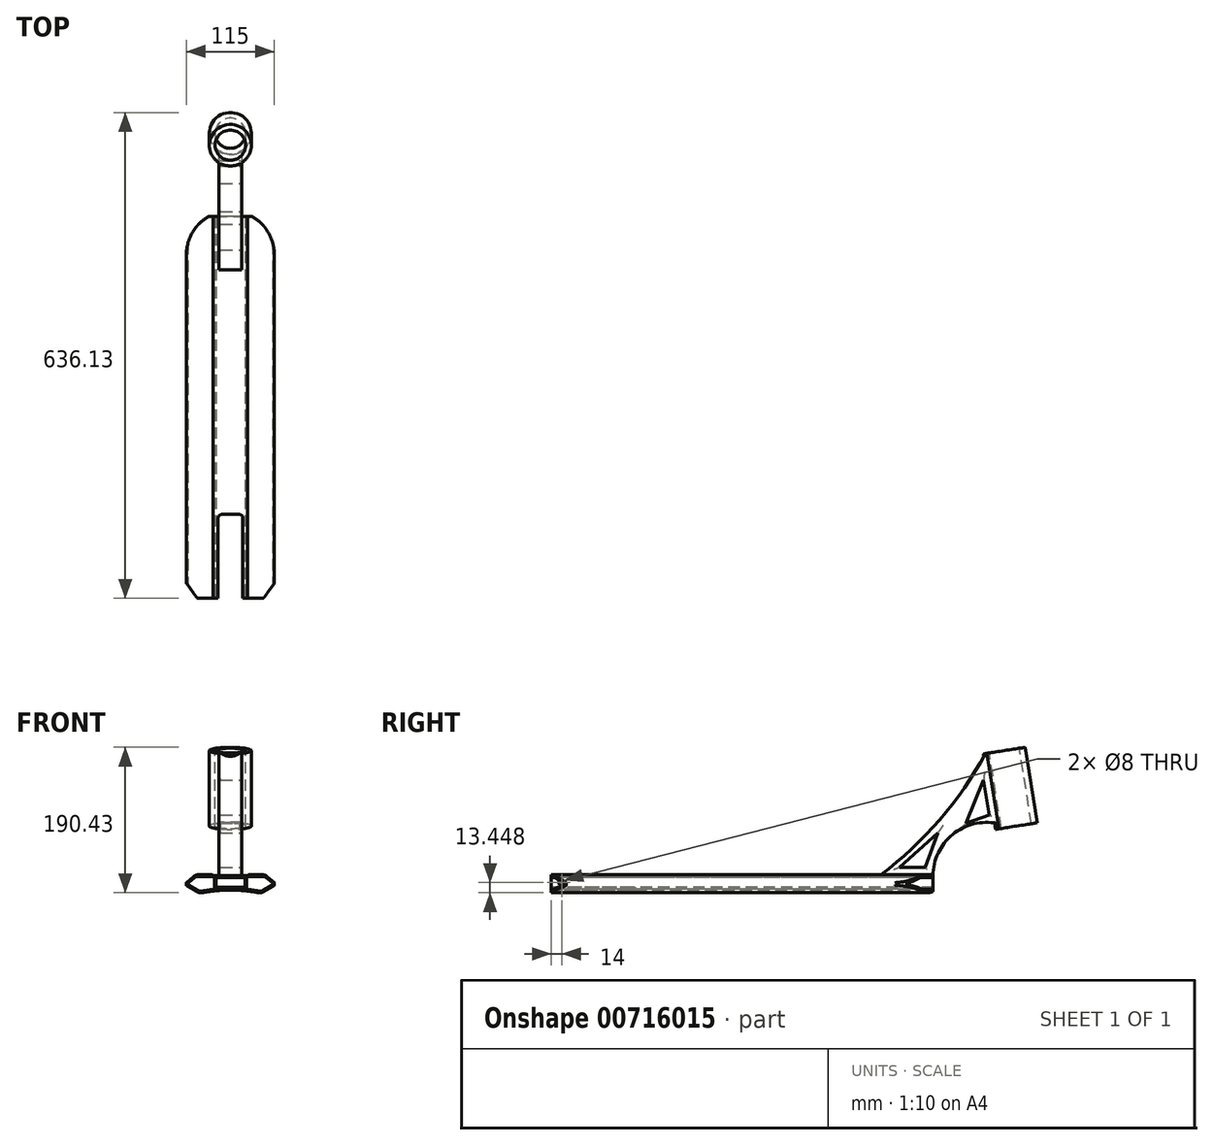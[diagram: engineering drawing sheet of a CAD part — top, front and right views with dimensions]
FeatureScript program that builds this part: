
annotation { "Feature Type Name" : "Feature", "Feature Type Description" : "" }
export const myFeature = defineFeature(function(context is Context, id is Id, definition is map)
    precondition{}
    {
        {
            var Q0;
            Q0=qCreatedBy(makeId("Front.planeOp"),FACE);
            var sketch = newSketch(context, id + "F0", { "sketchPlane" : qUnion([Q0])});
            skLineSegment(sketch, "E0", {"start": v(0, 0) * mm, "end": v(0, 25.65) * mm, "construction": true});
            skLineSegment(sketch, "E1", {"start": v(0, 15.2) * mm, "end": v(22.5, 15.2) * mm});
            skLineSegment(sketch, "E2", {"start": v(22.5, 15.2) * mm, "end": v(22.5, 16.5) * mm});
            skLineSegment(sketch, "E3", {"start": v(22.5, 16.5) * mm, "end": v(45.58, 16.5) * mm});
            skLineSegment(sketch, "E4", {"start": v(45.58, 16.5) * mm, "end": v(57.5, 6.5) * mm});
            skLineSegment(sketch, "E5", {"start": v(57.5, 6.5) * mm, "end": v(57.5, 2.5) * mm});
            skLineSegment(sketch, "E6", {"start": v(57.5, 2.5) * mm, "end": v(40.18, -7.5) * mm});
            skLineSegment(sketch, "E7.MirrorCS", {"start": v(0, 15.2) * mm, "end": v(-22.5, 15.2) * mm});
            skLineSegment(sketch, "E8.MirrorCS", {"start": v(-22.5, 16.5) * mm, "end": v(-45.58, 16.5) * mm});
            skLineSegment(sketch, "E9.MirrorCS", {"start": v(-45.58, 16.5) * mm, "end": v(-57.5, 6.5) * mm});
            skLineSegment(sketch, "E10.MirrorCS", {"start": v(-22.5, 15.2) * mm, "end": v(-22.5, 16.5) * mm});
            skLineSegment(sketch, "E11.MirrorCS", {"start": v(-57.5, 6.5) * mm, "end": v(-57.5, 2.5) * mm});
            skLineSegment(sketch, "E12.MirrorCS", {"start": v(-57.5, 2.5) * mm, "end": v(-40.18, -7.5) * mm});
            skArc(sketch, "E13", {"start": v(40.18, -7.5) * mm, "mid": v(0, -3.42) * mm, "end": v(-40.18, -7.5) * mm});
            skSolve(sketch);
        }
        {
            var Q0;
            Q0 = qSketchRegion(id + "F0", true);
            extrude(context, id + "F1", {"entities" : qUnion([Q0]), "depth" : 500 * mm, "offsetDistance" : 25 * mm, "symmetric" : true});
        }
        {
            var Q0;
            Q0=qCreatedBy(makeId("Front.planeOp"),FACE);
            var sketch = newSketch(context, id + "F2", { "sketchPlane" : qUnion([Q0])});
            skLineSegment(sketch, "E14.bottom", {"start": v(-19, 13.2) * mm, "end": v(19, 13.2) * mm});
            skLineSegment(sketch, "E14.top", {"start": v(-19, 0.2) * mm, "end": v(19, 0.2) * mm});
            skLineSegment(sketch, "E14.left", {"start": v(-19, 13.2) * mm, "end": v(-19, 0.2) * mm});
            skLineSegment(sketch, "E14.right", {"start": v(19, 13.2) * mm, "end": v(19, 0.2) * mm});
            skSolve(sketch);
        }
        {
            var Q0;
            Q0 = qSketchRegion(id + "F2", true);
            extrude(context, id + "F3", {"entities" : qUnion([Q0]), "operationType" : NewBodyOperationType.REMOVE, "oppositeDirection" : true, "depth" : 500 * mm, "offsetDistance" : 25 * mm, "symmetric" : true});
        }
        {
            var Q0;
            Q0=makeQuery(id+"F1.opExtrude","SWEPT_EDGE",EDGE,{"disambiguationData":[OSD([sQuery(id+"F0.wireOp",EDGE,"E8.MirrorCS"),sQuery(id+"F0.wireOp",EDGE,"E10.MirrorCS")])]});
            var Q1;
            Q1=makeQuery(id+"F1.opExtrude","SWEPT_EDGE",EDGE,{"disambiguationData":[OSD([sQuery(id+"F0.wireOp",EDGE,"E2"),sQuery(id+"F0.wireOp",EDGE,"E3")])]});
            fillet(context, id + "F4", {"entities" : qUnion([Q0, Q1]), "radius" : 2 * mm, "tangentPropagation" : true, "allowEdgeOverflow" : false});
        }
        {
            var Q0;
            Q0=makeQuery(id+"F1.opExtrude","SWEPT_EDGE",EDGE,{"disambiguationData":[OSD([sQuery(id+"F0.wireOp",EDGE,"E8.MirrorCS"),sQuery(id+"F0.wireOp",EDGE,"E9.MirrorCS")])]});
            var Q1;
            Q1=makeQuery(id+"F1.opExtrude","SWEPT_EDGE",EDGE,{"disambiguationData":[OSD([sQuery(id+"F0.wireOp",EDGE,"E3"),sQuery(id+"F0.wireOp",EDGE,"E4")])]});
            var Q2;
            Q2=makeQuery(id+"F1.opExtrude","SWEPT_EDGE",EDGE,{"disambiguationData":[OSD([sQuery(id+"F0.wireOp",EDGE,"E6"),sQuery(id+"F0.wireOp",EDGE,"E13")])]});
            var Q3;
            Q3=makeQuery(id+"F1.opExtrude","SWEPT_EDGE",EDGE,{"disambiguationData":[OSD([sQuery(id+"F0.wireOp",EDGE,"E12.MirrorCS"),sQuery(id+"F0.wireOp",EDGE,"E13")])]});
            fillet(context, id + "F5", {"entities" : qUnion([Q0, Q1, Q2, Q3]), "radius" : 9 * mm, "tangentPropagation" : true, "allowEdgeOverflow" : false});
        }
        {
            var Q0;
            Q0=makeQuery(id+"F1.opExtrude","SWEPT_EDGE",EDGE,{"disambiguationData":[OSD([sQuery(id+"F0.wireOp",EDGE,"E9.MirrorCS"),sQuery(id+"F0.wireOp",EDGE,"E11.MirrorCS")])]});
            var Q1;
            Q1=makeQuery(id+"F1.opExtrude","SWEPT_EDGE",EDGE,{"disambiguationData":[OSD([sQuery(id+"F0.wireOp",EDGE,"E11.MirrorCS"),sQuery(id+"F0.wireOp",EDGE,"E12.MirrorCS")])]});
            var Q2;
            Q2=makeQuery(id+"F1.opExtrude","SWEPT_EDGE",EDGE,{"disambiguationData":[OSD([sQuery(id+"F0.wireOp",EDGE,"E4"),sQuery(id+"F0.wireOp",EDGE,"E5")])]});
            var Q3;
            Q3=makeQuery(id+"F1.opExtrude","SWEPT_EDGE",EDGE,{"disambiguationData":[OSD([sQuery(id+"F0.wireOp",EDGE,"E5"),sQuery(id+"F0.wireOp",EDGE,"E6")])]});
            fillet(context, id + "F6", {"entities" : qUnion([Q0, Q1, Q2, Q3]), "radius" : 1 * mm, "tangentPropagation" : true, "allowEdgeOverflow" : false});
        }
        {
            var Q0;
            Q0=makeQuery(id+"F1.opExtrude","CAP_FACE",FACE,{"disambiguationData":[OSD([sQuery(id+"F0.wireOp",EDGE,"E1"),sQuery(id+"F0.wireOp",EDGE,"E2"),sQuery(id+"F0.wireOp",EDGE,"E3"),sQuery(id+"F0.wireOp",EDGE,"E4"),sQuery(id+"F0.wireOp",EDGE,"E5"),sQuery(id+"F0.wireOp",EDGE,"E6"),sQuery(id+"F0.wireOp",EDGE,"E7.MirrorCS"),sQuery(id+"F0.wireOp",EDGE,"E8.MirrorCS"),sQuery(id+"F0.wireOp",EDGE,"E9.MirrorCS"),sQuery(id+"F0.wireOp",EDGE,"E10.MirrorCS"),sQuery(id+"F0.wireOp",EDGE,"E11.MirrorCS"),sQuery(id+"F0.wireOp",EDGE,"E12.MirrorCS"),sQuery(id+"F0.wireOp",EDGE,"E13")])],"isStart":false});
            var sketch = newSketch(context, id + "F7", { "sketchPlane" : qUnion([Q0])});
            skLineSegment(sketch, "E15.0.0", {"start": v(-57.5, 6.04) * mm, "end": v(-57.5, 3.08) * mm});
            skArc(sketch, "E15.0.1", {"start": v(-57.5, 3.08) * mm, "mid": v(-57.37, 2.58) * mm, "end": v(-57, 2.22) * mm});
            skLineSegment(sketch, "E15.0.2", {"start": v(-57, 2.22) * mm, "end": v(-43.1, -5.8) * mm});
            skArc(sketch, "E15.0.3", {"start": v(-43.1, -5.8) * mm, "mid": v(-40.12, -6.88) * mm, "end": v(-36.94, -6.86) * mm});
            skArc(sketch, "E15.0.4", {"start": v(-36.94, -6.86) * mm, "mid": v(0, -3.42) * mm, "end": v(36.94, -6.86) * mm});
            skArc(sketch, "E15.0.5", {"start": v(36.94, -6.86) * mm, "mid": v(40.12, -6.88) * mm, "end": v(43.1, -5.8) * mm});
            skLineSegment(sketch, "E15.0.6", {"start": v(43.1, -5.8) * mm, "end": v(57, 2.22) * mm});
            skArc(sketch, "E15.0.7", {"start": v(57, 2.22) * mm, "mid": v(57.37, 2.58) * mm, "end": v(57.5, 3.08) * mm});
            skLineSegment(sketch, "E15.0.8", {"start": v(57.5, 3.08) * mm, "end": v(57.5, 6.04) * mm});
            skArc(sketch, "E15.0.9", {"start": v(57.5, 6.04) * mm, "mid": v(57.4, 6.46) * mm, "end": v(57.14, 6.8) * mm});
            skLineSegment(sketch, "E15.0.10", {"start": v(57.14, 6.8) * mm, "end": v(48.1, 14.4) * mm});
            skArc(sketch, "E15.0.11", {"start": v(48.1, 14.4) * mm, "mid": v(45.38, 15.96) * mm, "end": v(42.3, 16.5) * mm});
            skLineSegment(sketch, "E15.0.12", {"start": v(42.3, 16.5) * mm, "end": v(24.37, 16.5) * mm});
            skArc(sketch, "E15.0.13", {"start": v(24.37, 16.5) * mm, "mid": v(23.23, 16.15) * mm, "end": v(22.5, 15.2) * mm});
            skLineSegment(sketch, "E15.0.14", {"start": v(22.5, 15.2) * mm, "end": v(-22.5, 15.2) * mm});
            skArc(sketch, "E15.0.15", {"start": v(-22.5, 15.2) * mm, "mid": v(-23.23, 16.15) * mm, "end": v(-24.37, 16.5) * mm});
            skLineSegment(sketch, "E15.0.16", {"start": v(-24.37, 16.5) * mm, "end": v(-42.3, 16.5) * mm});
            skArc(sketch, "E15.0.17", {"start": v(-42.3, 16.5) * mm, "mid": v(-45.38, 15.96) * mm, "end": v(-48.1, 14.4) * mm});
            skLineSegment(sketch, "E15.0.18", {"start": v(-48.1, 14.4) * mm, "end": v(-57.14, 6.8) * mm});
            skArc(sketch, "E15.0.19", {"start": v(-57.14, 6.8) * mm, "mid": v(-57.4, 6.46) * mm, "end": v(-57.5, 6.04) * mm});
            skArc(sketch, "E16.0", {"start": v(-37.3, -4.9) * mm, "mid": v(0, -1.42) * mm, "end": v(37.3, -4.9) * mm});
            skArc(sketch, "E16.1", {"start": v(-42.1, -4.07) * mm, "mid": v(-39.78, -4.91) * mm, "end": v(-37.3, -4.9) * mm});
            skLineSegment(sketch, "E16.2", {"start": v(-24.37, 14.5) * mm, "end": v(-42.3, 14.5) * mm});
            skArc(sketch, "E16.3", {"start": v(-42.3, 14.5) * mm, "mid": v(-44.7, 14.08) * mm, "end": v(-46.8, 12.87) * mm});
            skLineSegment(sketch, "E16.4", {"start": v(-46.8, 12.87) * mm, "end": v(-54.66, 6.28) * mm});
            skLineSegment(sketch, "E16.5", {"start": v(-54.38, 3.01) * mm, "end": v(-42.1, -4.07) * mm});
            skLineSegment(sketch, "E17.0", {"start": v(-21, 15.2) * mm, "end": v(-21, -2.5) * mm});
            skLineSegment(sketch, "E17.1", {"start": v(-21, 15.2) * mm, "end": v(19, 15.2) * mm});
            skLineSegment(sketch, "E18.0", {"start": v(22.5, 13.2) * mm, "end": v(-22.5, 13.2) * mm});
            skArc(sketch, "E19", {"start": v(-22.5, 13.2) * mm, "mid": v(-23.23, 14.15) * mm, "end": v(-24.37, 14.5) * mm});
            skPoint(sketch, "E20.visualSharp", {"position": v(-56.85, 4.44) * mm});
            skArc(sketch, "E20.filletArc", {"start": v(-54.66, 6.28) * mm, "mid": v(-55.37, 4.57) * mm, "end": v(-54.38, 3.01) * mm});
            skLineSegment(sketch, "E21.MirrorCS", {"start": v(21, 15.2) * mm, "end": v(21, -2.5) * mm});
            skLineSegment(sketch, "E22.MirrorCS", {"start": v(24.37, 14.5) * mm, "end": v(42.3, 14.5) * mm});
            skArc(sketch, "E23.MirrorCS", {"start": v(42.3, 14.5) * mm, "mid": v(44.7, 14.08) * mm, "end": v(46.8, 12.87) * mm});
            skLineSegment(sketch, "E24.MirrorCS", {"start": v(46.8, 12.87) * mm, "end": v(54.66, 6.28) * mm});
            skArc(sketch, "E25.MirrorCS", {"start": v(54.66, 6.28) * mm, "mid": v(55.37, 4.57) * mm, "end": v(54.38, 3.01) * mm});
            skLineSegment(sketch, "E26.MirrorCS", {"start": v(54.38, 3.01) * mm, "end": v(42.1, -4.07) * mm});
            skArc(sketch, "E27.MirrorCS", {"start": v(42.1, -4.07) * mm, "mid": v(39.78, -4.91) * mm, "end": v(37.3, -4.9) * mm});
            skArc(sketch, "E28.MirrorCS", {"start": v(22.5, 13.2) * mm, "mid": v(23.23, 14.15) * mm, "end": v(24.37, 14.5) * mm});
            skSolve(sketch);
        }
        {
            var Q0;
            {var subQ4=sQuery(id+"F7.wireOp",EDGE,"E16.1");Q0=makeQuery(id+"F7.imprint","IMPRINT",FACE,{"disambiguationData":[TD([[makeQuery(id+"F7.imprint","IMPRINT",EDGE,{"derivedFrom":subQ4}),1.0]])]});}
            var Q1;
            Q1=makeQuery(id+"F7.imprint","IMPRINT",FACE,{"disambiguationData":[TD([[makeQuery(id+"F7.imprint","IMPRINT",EDGE,{"derivedFrom":sQuery(id+"F7.wireOp",EDGE,"E22.MirrorCS")}),-1.0]])]});
            extrude(context, id + "F8", {"entities" : qUnion([Q0, Q1]), "operationType" : NewBodyOperationType.REMOVE, "endBound" : BoundingType.THROUGH_ALL, "oppositeDirection" : true, "depth" : 25 * mm, "offsetDistance" : 25 * mm});
        }
        {
            var Q0;
            Q0=qCreatedBy(makeId("Top.planeOp"),FACE);
            var sketch = newSketch(context, id + "F9", { "sketchPlane" : qUnion([Q0])});
            skArc(sketch, "E29", {"start": v(57.5, 200) * mm, "mid": v(0, 257.5) * mm, "end": v(-57.5, 200) * mm});
            skLineSegment(sketch, "E30", {"start": v(-69.76, 280) * mm, "end": v(97.22, 280) * mm});
            skLineSegment(sketch, "E31", {"start": v(57.5, 200) * mm, "end": v(57.5, 280) * mm});
            skLineSegment(sketch, "E32", {"start": v(-57.5, 200) * mm, "end": v(-57.5, 280) * mm});
            skSolve(sketch);
        }
        {
            var Q0;
            Q0 = qSketchRegion(id + "F9", true);
            extrude(context, id + "F10", {"entities" : qUnion([Q0]), "operationType" : NewBodyOperationType.REMOVE, "endBound" : BoundingType.THROUGH_ALL, "oppositeDirection" : true, "depth" : 25 * mm, "offsetDistance" : 25 * mm, "hasSecondDirection" : true, "secondDirectionBound" : BoundingType.THROUGH_ALL, "secondDirectionOppositeDirection" : false, "secondDirectionDepth" : 25 * mm});
        }
        {
            var Q0;
            Q0=qCreatedBy(makeId("Top.planeOp"),FACE);
            var sketch = newSketch(context, id + "F11", { "sketchPlane" : qUnion([Q0])});
            skLineSegment(sketch, "E33", {"start": v(-68, -216) * mm, "end": v(-68, -346) * mm});
            skLineSegment(sketch, "E34", {"start": v(68, -346) * mm, "end": v(68, -216) * mm});
            skLineSegment(sketch, "E35", {"start": v(68, -216) * mm, "end": v(43.3, -250) * mm});
            skLineSegment(sketch, "E36", {"start": v(43.3, -250) * mm, "end": v(16.39, -250) * mm});
            skLineSegment(sketch, "E37", {"start": v(0.39, -140) * mm, "end": v(-16, -140) * mm});
            skLineSegment(sketch, "E38", {"start": v(-16, -140) * mm, "end": v(-16, -250) * mm});
            skLineSegment(sketch, "E39", {"start": v(-68, -216) * mm, "end": v(-43.3, -250) * mm});
            skLineSegment(sketch, "E40", {"start": v(-68, -346) * mm, "end": v(0, -346) * mm});
            skLineSegment(sketch, "E41", {"start": v(0, -346) * mm, "end": v(68, -346) * mm});
            skLineSegment(sketch, "E42", {"start": v(0.39, -140) * mm, "end": v(16.39, -140) * mm});
            skLineSegment(sketch, "E43", {"start": v(16.39, -140) * mm, "end": v(16.39, -250) * mm});
            skLineSegment(sketch, "E44", {"start": v(-43.3, -250) * mm, "end": v(-16, -250) * mm});
            skSolve(sketch);
        }
        {
            var Q0;
            Q0 = qSketchRegion(id + "F11", true);
            extrude(context, id + "F12", {"entities" : qUnion([Q0]), "operationType" : NewBodyOperationType.REMOVE, "endBound" : BoundingType.THROUGH_ALL, "depth" : 25 * mm, "offsetDistance" : 25 * mm, "hasSecondDirection" : true, "secondDirectionBound" : BoundingType.THROUGH_ALL, "secondDirectionOppositeDirection" : true, "secondDirectionDepth" : 25 * mm});
        }
        {
            var Q0;
            {var subQ0=sQuery(id+"F11.wireOp",EDGE,"E38");var subQ1=sQuery(id+"F11.wireOp",EDGE,"E37");Q0=makeQuery(id+"F12.boolean.opBoolean","COPY",EDGE,{"disambiguationData":[TD([makeQuery(id+"F3.boolean.opBoolean","COPY",FACE,{"derivedFrom":makeQuery(id+"F3.opExtrude","SWEPT_FACE",FACE,{"disambiguationData":[OSD([sQuery(id+"F2.wireOp",EDGE,"E14.bottom")])]})})])],"derivedFrom":makeQuery(id+"F12.opExtrude","SWEPT_EDGE",EDGE,{"disambiguationData":[OSD([subQ1,subQ0])]})});}
            var Q1;
            {var subQ0=sQuery(id+"F11.wireOp",EDGE,"E42");var subQ1=sQuery(id+"F11.wireOp",EDGE,"E43");Q1=makeQuery(id+"F12.boolean.opBoolean","COPY",EDGE,{"disambiguationData":[TD([makeQuery(id+"F3.boolean.opBoolean","COPY",FACE,{"derivedFrom":makeQuery(id+"F3.opExtrude","SWEPT_FACE",FACE,{"disambiguationData":[OSD([sQuery(id+"F2.wireOp",EDGE,"E14.bottom")])]})})])],"derivedFrom":makeQuery(id+"F12.opExtrude","SWEPT_EDGE",EDGE,{"disambiguationData":[OSD([subQ0,subQ1])]})});}
            var Q2;
            {var subQ2=sQuery(id+"F11.wireOp",EDGE,"E43");Q2=makeQuery(id+"F12.boolean.opBoolean","COPY",EDGE,{"disambiguationData":[TD([makeQuery(id+"F3.boolean.opBoolean","COPY",FACE,{"derivedFrom":makeQuery(id+"F3.opExtrude","SWEPT_FACE",FACE,{"disambiguationData":[OSD([sQuery(id+"F2.wireOp",EDGE,"E14.bottom")])]})})])],"derivedFrom":makeQuery(id+"F12.opExtrude","SWEPT_EDGE",EDGE,{"disambiguationData":[OSD([sQuery(id+"F11.wireOp",EDGE,"E36"),subQ2])]})});}
            var Q3;
            {var subQ2=sQuery(id+"F11.wireOp",EDGE,"E38");Q3=makeQuery(id+"F12.boolean.opBoolean","COPY",EDGE,{"disambiguationData":[TD([makeQuery(id+"F3.boolean.opBoolean","COPY",FACE,{"derivedFrom":makeQuery(id+"F3.opExtrude","SWEPT_FACE",FACE,{"disambiguationData":[OSD([sQuery(id+"F2.wireOp",EDGE,"E14.bottom")])]})})])],"derivedFrom":makeQuery(id+"F12.opExtrude","SWEPT_EDGE",EDGE,{"disambiguationData":[OSD([subQ2,sQuery(id+"F11.wireOp",EDGE,"E44")])]})});}
            var Q4;
            {var subQ0=sQuery(id+"F11.wireOp",EDGE,"E43");var subQ1=sQuery(id+"F11.wireOp",EDGE,"E42");Q4=makeQuery(id+"F12.boolean.opBoolean","COPY",EDGE,{"disambiguationData":[TD([makeQuery(id+"F1.opExtrude","SWEPT_FACE",FACE,{"disambiguationData":[OSD([sQuery(id+"F0.wireOp",EDGE,"E13")])]})])],"derivedFrom":makeQuery(id+"F12.opExtrude","SWEPT_EDGE",EDGE,{"disambiguationData":[OSD([subQ1,subQ0])]})});}
            var Q5;
            {var subQ0=sQuery(id+"F11.wireOp",EDGE,"E37");var subQ1=sQuery(id+"F11.wireOp",EDGE,"E38");Q5=makeQuery(id+"F12.boolean.opBoolean","COPY",EDGE,{"disambiguationData":[TD([makeQuery(id+"F1.opExtrude","SWEPT_FACE",FACE,{"disambiguationData":[OSD([sQuery(id+"F0.wireOp",EDGE,"E13")])]})])],"derivedFrom":makeQuery(id+"F12.opExtrude","SWEPT_EDGE",EDGE,{"disambiguationData":[OSD([subQ0,subQ1])]})});}
            fillet(context, id + "F13", {"entities" : qUnion([Q0, Q1, Q2, Q3, Q4, Q5]), "radius" : 5 * mm, "tangentPropagation" : true, "allowEdgeOverflow" : false});
        }
        {
            var Q0;
            Q0=qCreatedBy(makeId("Right.planeOp"),FACE);
            var sketch = newSketch(context, id + "F14", { "sketchPlane" : qUnion([Q0])});
            skLineSegment(sketch, "E45", {"start": v(180, 16.5) * mm, "end": v(250, 16.5) * mm});
            skLineSegment(sketch, "E46", {"start": v(333.69, 85.16) * mm, "end": v(334.85, 77.83) * mm});
            skLineSegment(sketch, "E47", {"start": v(334.85, 77.83) * mm, "end": v(381.69, 85.25) * mm});
            skArc(sketch, "E48", {"start": v(333.69, 85.16) * mm, "mid": v(275.6, 70.63) * mm, "end": v(250, 16.5) * mm});
            skLineSegment(sketch, "E49", {"start": v(381.69, 85.25) * mm, "end": v(366.04, 184.02) * mm});
            skLineSegment(sketch, "E50", {"start": v(366.04, 184.02) * mm, "end": v(318.63, 176.5) * mm});
            skArc(sketch, "E51", {"start": v(180, 16.5) * mm, "mid": v(257.88, 89.09) * mm, "end": v(318.63, 176.5) * mm});
            skSolve(sketch);
        }
        {
            var Q0;
            Q0 = qSketchRegion(id + "F14", true);
            extrude(context, id + "F15", {"entities" : qUnion([Q0]), "operationType" : NewBodyOperationType.ADD, "depth" : 30 * mm, "offsetDistance" : 25 * mm, "symmetric" : true});
        }
        {
            var Q0;
            Q0=makeQuery(id+"F15.opExtrude","SWEPT_FACE",FACE,{"disambiguationData":[OSD([sQuery(id+"F14.wireOp",EDGE,"E50")])]});
            var sketch = newSketch(context, id + "F16", { "sketchPlane" : qUnion([Q0])});
            skCircle(sketch, "E52", {"center": v(0, 367.32) * mm, "radius": 27.5 * mm});
            skSolve(sketch);
        }
        {
            var Q0;
            Q0 = qSketchRegion(id + "F16", true);
            var Q1;
            Q1=makeQuery(id+"F15.opExtrude","SWEPT_FACE",FACE,{"disambiguationData":[OSD([sQuery(id+"F14.wireOp",EDGE,"E47")])]});
            extrude(context, id + "F17", {"entities" : qUnion([Q0]), "operationType" : NewBodyOperationType.ADD, "endBound" : BoundingType.UP_TO_SURFACE, "oppositeDirection" : true, "depth" : 25 * mm, "endBoundEntityFace" : qUnion([Q1]), "offsetDistance" : 25 * mm});
        }
        {
            var Q0;
            Q0=makeQuery(id+"F17.boolean.opBoolean","MERGE",FACE,{"derivedFrom":[makeQuery(id+"F15.opExtrude","SWEPT_FACE",FACE,{"disambiguationData":[OSD([sQuery(id+"F14.wireOp",EDGE,"E50")])]}),makeQuery(id+"F17.opExtrude","CAP_FACE",FACE,{"disambiguationData":[OSD([sQuery(id+"F16.wireOp",EDGE,"E52")])],"isStart":true})]});
            var sketch = newSketch(context, id + "F18", { "sketchPlane" : qUnion([Q0])});
            skPoint(sketch, "E53", {"position": v(0, 367.32) * mm});
            skSolve(sketch);
        }
        {
            var Q0;
            Q0=sQuery(id+"F18.wireOp",VERTEX,"E53");
            var Q1;
            Q1=makeQuery(id+"F15.opExtrude","SWEPT_BODY",BODY,{"disambiguationData":[OSD([sQuery(id+"F14.wireOp",EDGE,"E45"),sQuery(id+"F14.wireOp",EDGE,"E46"),sQuery(id+"F14.wireOp",EDGE,"E47"),sQuery(id+"F14.wireOp",EDGE,"E48"),sQuery(id+"F14.wireOp",EDGE,"E49"),sQuery(id+"F14.wireOp",EDGE,"E50"),sQuery(id+"F14.wireOp",EDGE,"E51")])]});
            hole(context, id + "F19", {"style" : HoleStyle.SIMPLE, "endStyle" : HoleEndStyle.THROUGH, "holeDiameter" : 40 * mm, "majorDiameter" : 5 * mm, "isTappedThrough" : true, "tappedDepth" : 12 * mm, "tapClearance" : 3, "locations" : qUnion([Q0]), "scope" : qUnion([Q1])});
        }
        {
            var Q0;
            Q0=makeQuery(id+"F15.opExtrude","SWEPT_FACE",FACE,{"disambiguationData":[OSD([sQuery(id+"F14.wireOp",EDGE,"E45")])]});
            var Q1;
            Q1=makeQuery(id+"F1.opExtrude","SWEPT_FACE",FACE,{"disambiguationData":[OSD([sQuery(id+"F0.wireOp",EDGE,"E1"),sQuery(id+"F0.wireOp",EDGE,"E7.MirrorCS")])]});
            extrude(context, id + "F20", {"entities" : qUnion([Q0]), "endBound" : BoundingType.UP_TO_SURFACE, "depth" : 25 * mm, "endBoundEntityFace" : qUnion([Q1]), "offsetDistance" : 25 * mm});
        }
        {
            var Q0;
            Q0=makeQuery(id+"F20.opExtrude","SWEPT_BODY",BODY,{"disambiguationData":[OSD([sQuery(id+"F14.wireOp",EDGE,"E45")])]});
            deleteBodies(context, id + "F21", {"entities" : qUnion([Q0])});
        }
        {
            var Q0;
            Q0=makeQuery(id+"F15.opExtrude","SWEPT_BODY",BODY,{"disambiguationData":[OSD([sQuery(id+"F14.wireOp",EDGE,"E45"),sQuery(id+"F14.wireOp",EDGE,"E46"),sQuery(id+"F14.wireOp",EDGE,"E47"),sQuery(id+"F14.wireOp",EDGE,"E48"),sQuery(id+"F14.wireOp",EDGE,"E49"),sQuery(id+"F14.wireOp",EDGE,"E50"),sQuery(id+"F14.wireOp",EDGE,"E51")])]});
            transform(context, id + "F22", {"entities" : qUnion([Q0]), "transformType" : TransformType.TRANSLATION_3D, "dx" : 0 * mm, "dy" : 0 * mm, "dz" : -1.3 * mm, "makeCopy" : false});
        }
        {
            var Q0;
            Q0=makeQuery(id+"F8.boolean.opBoolean","COPY",FACE,{"derivedFrom":makeQuery(id+"F8.opExtrude","SWEPT_FACE",FACE,{"disambiguationData":[OSD([sQuery(id+"F7.wireOp",EDGE,"E21.MirrorCS")])]})});
            var sketch = newSketch(context, id + "F23", { "sketchPlane" : qUnion([Q0])});
            skPoint(sketch, "E54", {"position": v(-236, 6.44) * mm});
            skSolve(sketch);
        }
        {
            var Q0;
            Q0=sQuery(id+"F23.wireOp",VERTEX,"E54");
            var Q1;
            Q1=makeQuery(id+"F1.opExtrude","SWEPT_BODY",BODY,{"disambiguationData":[OSD([sQuery(id+"F0.wireOp",EDGE,"E1"),sQuery(id+"F0.wireOp",EDGE,"E2"),sQuery(id+"F0.wireOp",EDGE,"E3"),sQuery(id+"F0.wireOp",EDGE,"E4"),sQuery(id+"F0.wireOp",EDGE,"E5"),sQuery(id+"F0.wireOp",EDGE,"E6"),sQuery(id+"F0.wireOp",EDGE,"E7.MirrorCS"),sQuery(id+"F0.wireOp",EDGE,"E8.MirrorCS"),sQuery(id+"F0.wireOp",EDGE,"E9.MirrorCS"),sQuery(id+"F0.wireOp",EDGE,"E10.MirrorCS"),sQuery(id+"F0.wireOp",EDGE,"E11.MirrorCS"),sQuery(id+"F0.wireOp",EDGE,"E12.MirrorCS"),sQuery(id+"F0.wireOp",EDGE,"E13")])]});
            hole(context, id + "F24", {"style" : HoleStyle.SIMPLE, "endStyle" : HoleEndStyle.BLIND, "holeDiameter" : 8 * mm, "majorDiameter" : 5 * mm, "holeDepth" : 50 * mm, "isTappedThrough" : true, "tappedDepth" : 12 * mm, "tapClearance" : 3, "locations" : qUnion([Q0]), "scope" : qUnion([Q1])});
        }
        {
            var Q0;
            Q0=makeQuery(id+"F15.opExtrude","CAP_FACE",FACE,{"disambiguationData":[OSD([sQuery(id+"F14.wireOp",EDGE,"E45"),sQuery(id+"F14.wireOp",EDGE,"E46"),sQuery(id+"F14.wireOp",EDGE,"E47"),sQuery(id+"F14.wireOp",EDGE,"E48"),sQuery(id+"F14.wireOp",EDGE,"E49"),sQuery(id+"F14.wireOp",EDGE,"E50"),sQuery(id+"F14.wireOp",EDGE,"E51")])],"isStart":false});
            var sketch = newSketch(context, id + "F25", { "sketchPlane" : qUnion([Q0])});
            skLineSegment(sketch, "E55", {"start": v(206, 26.5) * mm, "end": v(256.38, 71.5) * mm});
            skLineSegment(sketch, "E56", {"start": v(256.38, 71.5) * mm, "end": v(240, 26.5) * mm});
            skLineSegment(sketch, "E57", {"start": v(240, 26.5) * mm, "end": v(206, 26.5) * mm});
            skLineSegment(sketch, "E58", {"start": v(316.02, 140.25) * mm, "end": v(323.2, 94.93) * mm});
            skLineSegment(sketch, "E59", {"start": v(323.2, 94.93) * mm, "end": v(293.2, 83.86) * mm});
            skLineSegment(sketch, "E60", {"start": v(293.2, 83.86) * mm, "end": v(316.02, 140.25) * mm});
            skSolve(sketch);
        }
        {
            var Q0;
            Q0=makeQuery(id+"F25.imprint","IMPRINT",FACE,{"disambiguationData":[TD([[makeQuery(id+"F25.imprint","IMPRINT",EDGE,{"derivedFrom":sQuery(id+"F25.wireOp",EDGE,"E58")}),-1.0]])]});
            var Q1;
            Q1=makeQuery(id+"F25.imprint","IMPRINT",FACE,{"disambiguationData":[TD([[makeQuery(id+"F25.imprint","IMPRINT",EDGE,{"derivedFrom":sQuery(id+"F25.wireOp",EDGE,"E55")}),-1.0]])]});
            extrude(context, id + "F26", {"entities" : qUnion([Q0, Q1]), "operationType" : NewBodyOperationType.REMOVE, "endBound" : BoundingType.THROUGH_ALL, "oppositeDirection" : true, "depth" : 25 * mm, "offsetDistance" : 25 * mm});
        }
        {
            var Q0;
            Q0=makeQuery(id+"F26.boolean.opBoolean","COPY",EDGE,{"derivedFrom":makeQuery(id+"F26.opExtrude","CAP_EDGE",EDGE,{"disambiguationData":[OSD([sQuery(id+"F25.wireOp",EDGE,"E59")])],"isStart":true})});
            var Q1;
            Q1=makeQuery(id+"F26.boolean.opBoolean","COPY",EDGE,{"derivedFrom":makeQuery(id+"F26.opExtrude","CAP_EDGE",EDGE,{"disambiguationData":[OSD([sQuery(id+"F25.wireOp",EDGE,"E58")])],"isStart":true})});
            var Q2;
            Q2=makeQuery(id+"F26.boolean.opBoolean","COPY",EDGE,{"derivedFrom":makeQuery(id+"F26.opExtrude","CAP_EDGE",EDGE,{"disambiguationData":[OSD([sQuery(id+"F25.wireOp",EDGE,"E60")])],"isStart":true})});
            var Q3;
            Q3=makeQuery(id+"F26.boolean.opBoolean","INTERSECT",EDGE,{"derivedFrom":[makeQuery(id+"F15.opExtrude","CAP_FACE",FACE,{"disambiguationData":[OSD([sQuery(id+"F14.wireOp",EDGE,"E45"),sQuery(id+"F14.wireOp",EDGE,"E46"),sQuery(id+"F14.wireOp",EDGE,"E47"),sQuery(id+"F14.wireOp",EDGE,"E48"),sQuery(id+"F14.wireOp",EDGE,"E49"),sQuery(id+"F14.wireOp",EDGE,"E50"),sQuery(id+"F14.wireOp",EDGE,"E51")])],"isStart":true}),makeQuery(id+"F26.opExtrude","SWEPT_FACE",FACE,{"disambiguationData":[OSD([sQuery(id+"F25.wireOp",EDGE,"E59")])]})]});
            var Q4;
            Q4=makeQuery(id+"F26.boolean.opBoolean","INTERSECT",EDGE,{"derivedFrom":[makeQuery(id+"F15.opExtrude","CAP_FACE",FACE,{"disambiguationData":[OSD([sQuery(id+"F14.wireOp",EDGE,"E45"),sQuery(id+"F14.wireOp",EDGE,"E46"),sQuery(id+"F14.wireOp",EDGE,"E47"),sQuery(id+"F14.wireOp",EDGE,"E48"),sQuery(id+"F14.wireOp",EDGE,"E49"),sQuery(id+"F14.wireOp",EDGE,"E50"),sQuery(id+"F14.wireOp",EDGE,"E51")])],"isStart":true}),makeQuery(id+"F26.opExtrude","SWEPT_FACE",FACE,{"disambiguationData":[OSD([sQuery(id+"F25.wireOp",EDGE,"E60")])]})]});
            var Q5;
            Q5=makeQuery(id+"F26.boolean.opBoolean","INTERSECT",EDGE,{"derivedFrom":[makeQuery(id+"F15.opExtrude","CAP_FACE",FACE,{"disambiguationData":[OSD([sQuery(id+"F14.wireOp",EDGE,"E45"),sQuery(id+"F14.wireOp",EDGE,"E46"),sQuery(id+"F14.wireOp",EDGE,"E47"),sQuery(id+"F14.wireOp",EDGE,"E48"),sQuery(id+"F14.wireOp",EDGE,"E49"),sQuery(id+"F14.wireOp",EDGE,"E50"),sQuery(id+"F14.wireOp",EDGE,"E51")])],"isStart":true}),makeQuery(id+"F26.opExtrude","SWEPT_FACE",FACE,{"disambiguationData":[OSD([sQuery(id+"F25.wireOp",EDGE,"E58")])]})]});
            var Q6;
            Q6=makeQuery(id+"F26.boolean.opBoolean","INTERSECT",EDGE,{"derivedFrom":[makeQuery(id+"F15.opExtrude","CAP_FACE",FACE,{"disambiguationData":[OSD([sQuery(id+"F14.wireOp",EDGE,"E45"),sQuery(id+"F14.wireOp",EDGE,"E46"),sQuery(id+"F14.wireOp",EDGE,"E47"),sQuery(id+"F14.wireOp",EDGE,"E48"),sQuery(id+"F14.wireOp",EDGE,"E49"),sQuery(id+"F14.wireOp",EDGE,"E50"),sQuery(id+"F14.wireOp",EDGE,"E51")])],"isStart":true}),makeQuery(id+"F26.opExtrude","SWEPT_FACE",FACE,{"disambiguationData":[OSD([sQuery(id+"F25.wireOp",EDGE,"E55")])]})]});
            var Q7;
            Q7=makeQuery(id+"F26.boolean.opBoolean","INTERSECT",EDGE,{"derivedFrom":[makeQuery(id+"F15.opExtrude","CAP_FACE",FACE,{"disambiguationData":[OSD([sQuery(id+"F14.wireOp",EDGE,"E45"),sQuery(id+"F14.wireOp",EDGE,"E46"),sQuery(id+"F14.wireOp",EDGE,"E47"),sQuery(id+"F14.wireOp",EDGE,"E48"),sQuery(id+"F14.wireOp",EDGE,"E49"),sQuery(id+"F14.wireOp",EDGE,"E50"),sQuery(id+"F14.wireOp",EDGE,"E51")])],"isStart":true}),makeQuery(id+"F26.opExtrude","SWEPT_FACE",FACE,{"disambiguationData":[OSD([sQuery(id+"F25.wireOp",EDGE,"E57")])]})]});
            var Q8;
            Q8=makeQuery(id+"F26.boolean.opBoolean","INTERSECT",EDGE,{"derivedFrom":[makeQuery(id+"F15.opExtrude","CAP_FACE",FACE,{"disambiguationData":[OSD([sQuery(id+"F14.wireOp",EDGE,"E45"),sQuery(id+"F14.wireOp",EDGE,"E46"),sQuery(id+"F14.wireOp",EDGE,"E47"),sQuery(id+"F14.wireOp",EDGE,"E48"),sQuery(id+"F14.wireOp",EDGE,"E49"),sQuery(id+"F14.wireOp",EDGE,"E50"),sQuery(id+"F14.wireOp",EDGE,"E51")])],"isStart":true}),makeQuery(id+"F26.opExtrude","SWEPT_FACE",FACE,{"disambiguationData":[OSD([sQuery(id+"F25.wireOp",EDGE,"E56")])]})]});
            var Q9;
            Q9=makeQuery(id+"F26.boolean.opBoolean","COPY",EDGE,{"derivedFrom":makeQuery(id+"F26.opExtrude","CAP_EDGE",EDGE,{"disambiguationData":[OSD([sQuery(id+"F25.wireOp",EDGE,"E55")])],"isStart":true})});
            var Q10;
            Q10=makeQuery(id+"F26.boolean.opBoolean","COPY",EDGE,{"derivedFrom":makeQuery(id+"F26.opExtrude","CAP_EDGE",EDGE,{"disambiguationData":[OSD([sQuery(id+"F25.wireOp",EDGE,"E56")])],"isStart":true})});
            var Q11;
            Q11=makeQuery(id+"F26.boolean.opBoolean","COPY",EDGE,{"derivedFrom":makeQuery(id+"F26.opExtrude","CAP_EDGE",EDGE,{"disambiguationData":[OSD([sQuery(id+"F25.wireOp",EDGE,"E57")])],"isStart":true})});
            fillet(context, id + "F27", {"entities" : qUnion([Q0, Q1, Q2, Q3, Q4, Q5, Q6, Q7, Q8, Q9, Q10, Q11]), "radius" : 3 * mm, "tangentPropagation" : true, "defaultsChanged" : false, "vertexSettings" : [], "allowEdgeOverflow" : false});
        }
    });
